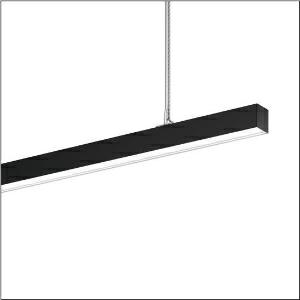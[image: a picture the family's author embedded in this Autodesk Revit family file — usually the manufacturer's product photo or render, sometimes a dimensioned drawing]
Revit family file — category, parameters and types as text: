
# Revit family: silica_r__21_51mx33db39bb_fd0d
name_source: partatom
category: Lighting Fixtures
units: mm (PartAtom-declared; Revit-internal decimal feet)

## family parameters
Cut with Voids When Loaded = No
Host = Face
Light Source = No
Part Type = Normal
Room Calculation Point = No
Round Connector Dimension = Use Diameter
Shared = No

## types (1)
- --- (1 x LED, 7390 lm, 51.6 W, 3000K)
    Apparent Load = 52 VA
    CIE Flux Codes = 78 96 99 55 100
    Color Rendering = 80
    Color Temperature = 3000K
    Default Elevation = 1800 mm
    Description = Silica® 21, office luminaire, primary optical cover: prismatic diffuser, of PMMA, CAT 2 (L<= 3000cd/m²), light emission: direct/indirect distribution, primary light characteristic: symmetric, installation type: suspended mounting, LED, rated luminous flux: 7.390lm, luminous efficacy: 143lm/W, light colour: 830, colour temperature: 3000K, with terminal, 3+2-pole, max. 2.5mm², mains connection: 220..240V, AC, 50/60Hz, rated input power: 51.6W, luminaire housing, of aluminium, jet black (RAL 9005), length: 1.504mm, width: 53mm, height: 53mm, protection rating (complete): IP20, insulation class (complete): insulation class I (protective earthing), certification: CE, permissible operating ambient temperature: 0..+35°C, standard: EN 50419, packaging unit: 1 piece
    Height = 53 mm
    Lamp = 1 x LED
    Lamp Light Flux = 7390 lm
    Lamp Power = 51.6 W
    Lamp count = 1
    Length = 1504 mm
    Luminous efficacy = 143 lm/W
    Manufacturer = Siteco
    ModVariant = No
    Model = 51MX33DB39BB
    Mounting Place = Ceiling
    Mounting Type = Pendant
    Number of Poles = 1
    OnlyDefault = Yes
    Power Factor = 1
    Product Name = Silica® 21
    Product group = office luminaire | ceiling pendant
    ProductGroupID = 902
    Protection Class = Protection class I
    Protection Degree = IP 20
    RLX_Detail_Level = 1
    RLX_Emergency_Light_Flux = 0 lm
    RLX_Emergency_Type = 0
    RLX_Emergency_Type_DB = No
    RlxData = <blob elided: 26097 chars, md5=120f1979>
    Socket = socket
    Standby Power = 0 W
    System Light Flux = 7390 lm
    System Power = 52 W
    Type Comments = factory setting: luminous flux: 100 % | dim-lin: 254 | 345 mA
    Type Image = l_1335856.jpg
    URL = http://relux.com
    VarID = @adj_087545
    Voltage = 0 V
    Weight = 0.00 kg
    Width = 53 mm

## geometry (parser evidence)
native form markers: Blend x4, Sweep x12
no freeform markers — native parametric forms only
